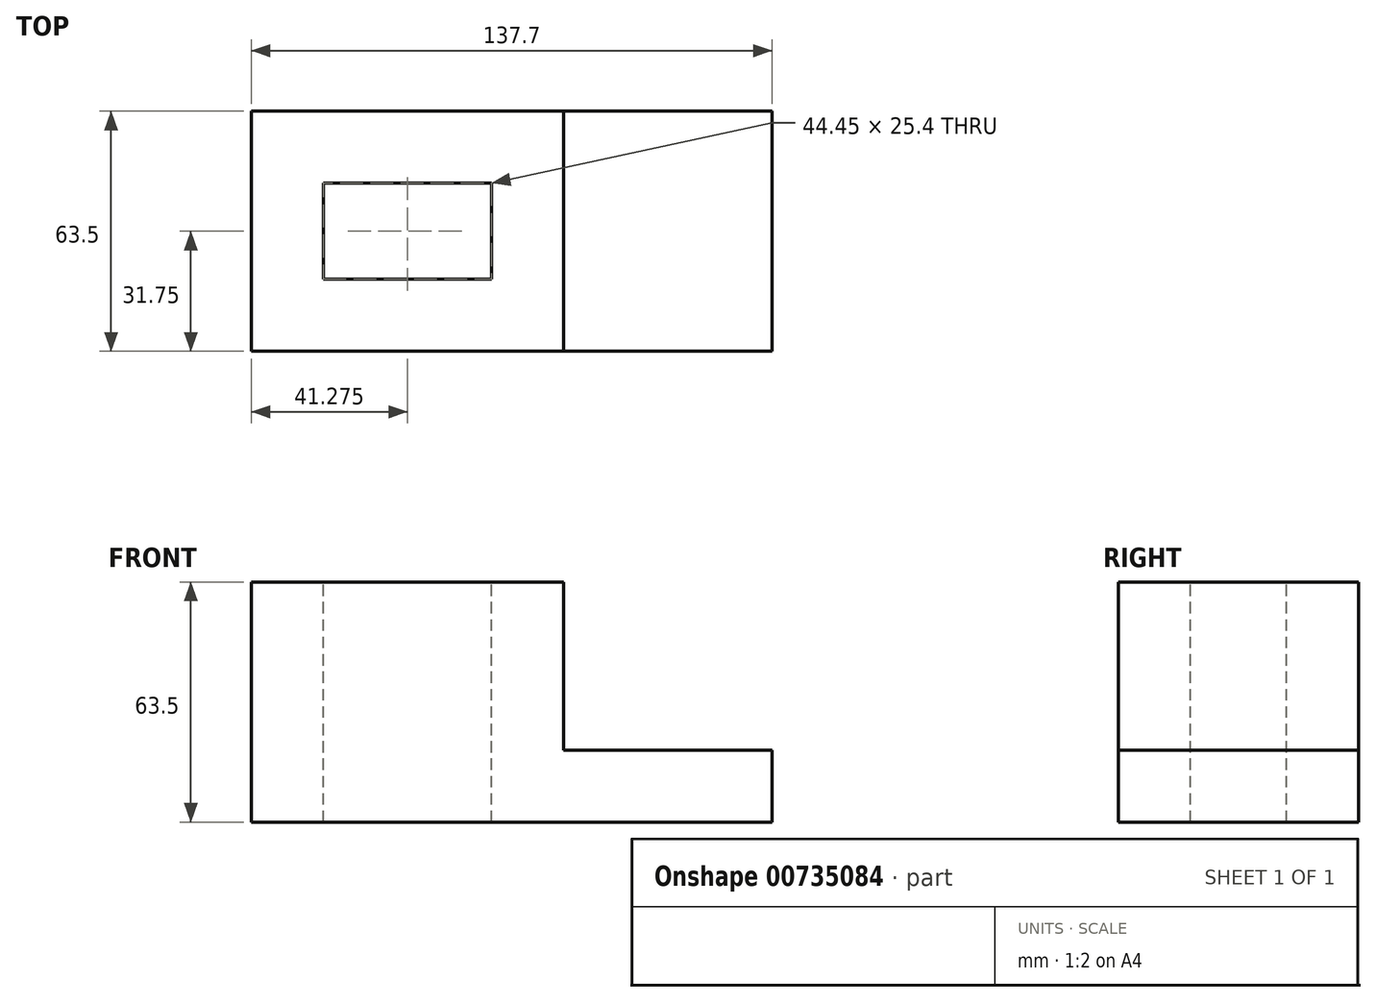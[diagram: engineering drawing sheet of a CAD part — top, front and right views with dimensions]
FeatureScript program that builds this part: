
annotation { "Feature Type Name" : "Feature", "Feature Type Description" : "" }
export const myFeature = defineFeature(function(context is Context, id is Id, definition is map)
    precondition{}
    {
        {
            var Q0;
            Q0=qCreatedBy(makeId("Top.planeOp"),FACE);
            var sketch = newSketch(context, id + "F0", { "sketchPlane" : qUnion([Q0])});
            skLineSegment(sketch, "E0.bottom", {"start": v(0, 0) * mm, "end": v(-82.55, 0) * mm});
            skLineSegment(sketch, "E0.top", {"start": v(0, 63.5) * mm, "end": v(-82.55, 63.5) * mm});
            skLineSegment(sketch, "E0.left", {"start": v(0, 0) * mm, "end": v(0, 63.5) * mm});
            skLineSegment(sketch, "E0.right", {"start": v(-82.55, 0) * mm, "end": v(-82.55, 63.5) * mm});
            skLineSegment(sketch, "E1.bottom", {"start": v(0, 0) * mm, "end": v(55.15, 0) * mm});
            skLineSegment(sketch, "E1.top", {"start": v(0, 63.5) * mm, "end": v(55.15, 63.5) * mm});
            skLineSegment(sketch, "E1.right", {"start": v(55.15, 0) * mm, "end": v(55.15, 63.5) * mm});
            skSolve(sketch);
        }
        {
            var Q0;
            Q0=makeQuery(id+"F0.imprint","IMPRINT",FACE,{"disambiguationData":[TD([[makeQuery(id+"F0.imprint","IMPRINT",EDGE,{"derivedFrom":sQuery(id+"F0.wireOp",EDGE,"E0.bottom")}),-1.0]])]});
            extrude(context, id + "F1", {"entities" : qUnion([Q0]), "depth" : 63.5 * mm, "offsetDistance" : 25.4 * mm});
        }
        {
            var Q0;
            Q0=makeQuery(id+"F0.imprint","IMPRINT",FACE,{"disambiguationData":[TD([[makeQuery(id+"F0.imprint","IMPRINT",EDGE,{"derivedFrom":sQuery(id+"F0.wireOp",EDGE,"E1.bottom")}),1.0]])]});
            extrude(context, id + "F2", {"entities" : qUnion([Q0]), "operationType" : NewBodyOperationType.ADD, "depth" : 19.05 * mm, "offsetDistance" : 25.4 * mm});
        }
        {
            var Q0;
            Q0=makeQuery(id+"F1.opExtrude","CAP_FACE",FACE,{"disambiguationData":[OSD([sQuery(id+"F0.wireOp",EDGE,"E0.bottom"),sQuery(id+"F0.wireOp",EDGE,"E0.top"),sQuery(id+"F0.wireOp",EDGE,"E0.right"),sQuery(id+"F0.wireOp",EDGE,"E0.left")])],"isStart":false});
            var sketch = newSketch(context, id + "F3", { "sketchPlane" : qUnion([Q0])});
            skLineSegment(sketch, "E2", {"start": v(-82.55, 31.75) * mm, "end": v(-63.5, 31.75) * mm, "construction": true});
            skLineSegment(sketch, "E3", {"start": v(-41.28, 0) * mm, "end": v(-41.28, 19.05) * mm, "construction": true});
            skLineSegment(sketch, "E4", {"start": v(0, 31.75) * mm, "end": v(-19.05, 31.75) * mm, "construction": true});
            skLineSegment(sketch, "E5", {"start": v(-41.28, 63.5) * mm, "end": v(-41.28, 44.45) * mm, "construction": true});
            skLineSegment(sketch, "E6", {"start": v(-63.5, 31.75) * mm, "end": v(-63.5, 44.45) * mm});
            skLineSegment(sketch, "E7", {"start": v(-63.5, 44.45) * mm, "end": v(-41.28, 44.45) * mm});
            skLineSegment(sketch, "E8", {"start": v(-41.28, 44.45) * mm, "end": v(-19.05, 44.45) * mm});
            skLineSegment(sketch, "E9", {"start": v(-19.05, 44.45) * mm, "end": v(-19.05, 31.75) * mm});
            skLineSegment(sketch, "E10", {"start": v(-19.05, 19.05) * mm, "end": v(-19.05, 31.75) * mm});
            skLineSegment(sketch, "E11", {"start": v(-19.05, 19.05) * mm, "end": v(-41.28, 19.05) * mm});
            skLineSegment(sketch, "E12", {"start": v(-41.28, 19.05) * mm, "end": v(-63.5, 19.05) * mm});
            skLineSegment(sketch, "E13", {"start": v(-63.5, 31.75) * mm, "end": v(-63.5, 19.05) * mm});
            skSolve(sketch);
        }
        {
            var Q0;
            Q0=makeQuery(id+"F3.imprint","IMPRINT",FACE,{"disambiguationData":[TD([[makeQuery(id+"F3.imprint","IMPRINT",EDGE,{"derivedFrom":sQuery(id+"F3.wireOp",EDGE,"E6")}),-1.0]])]});
            extrude(context, id + "F4", {"entities" : qUnion([Q0]), "operationType" : NewBodyOperationType.REMOVE, "endBound" : BoundingType.THROUGH_ALL, "oppositeDirection" : true, "depth" : 25.4 * mm, "offsetDistance" : 25.4 * mm});
        }
    });
